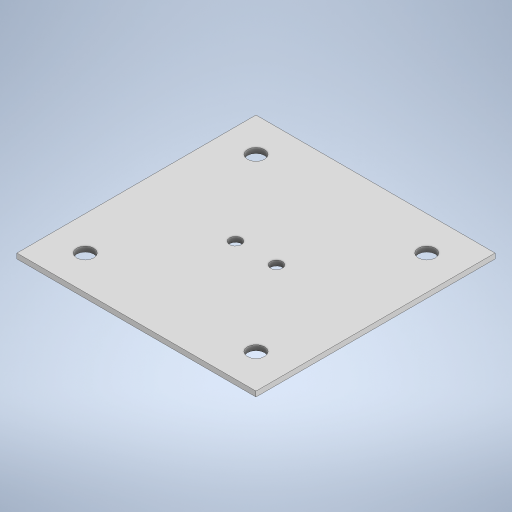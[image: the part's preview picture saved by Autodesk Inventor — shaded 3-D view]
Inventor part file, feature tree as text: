
AUTODESK INVENTOR PART (.ipt)
format: ipt  version: 2023 (Build 270158000, 158)  size: 230,912 bytes
history: native  units: mm
features: other x1, extrude x1, sketch x1
ambient origin geometry x8: Origin, YZ Plane, XZ Plane, XY Plane, X Axis, Y Axis, Z Axis, Center Point
bodies: Body1 (feature_tree)
feature tree (3):
  other  "Твердое тело1"
  extrude  "Выдавливание1"  Depth=140.0mm
  sketch  "Эскиз1"
